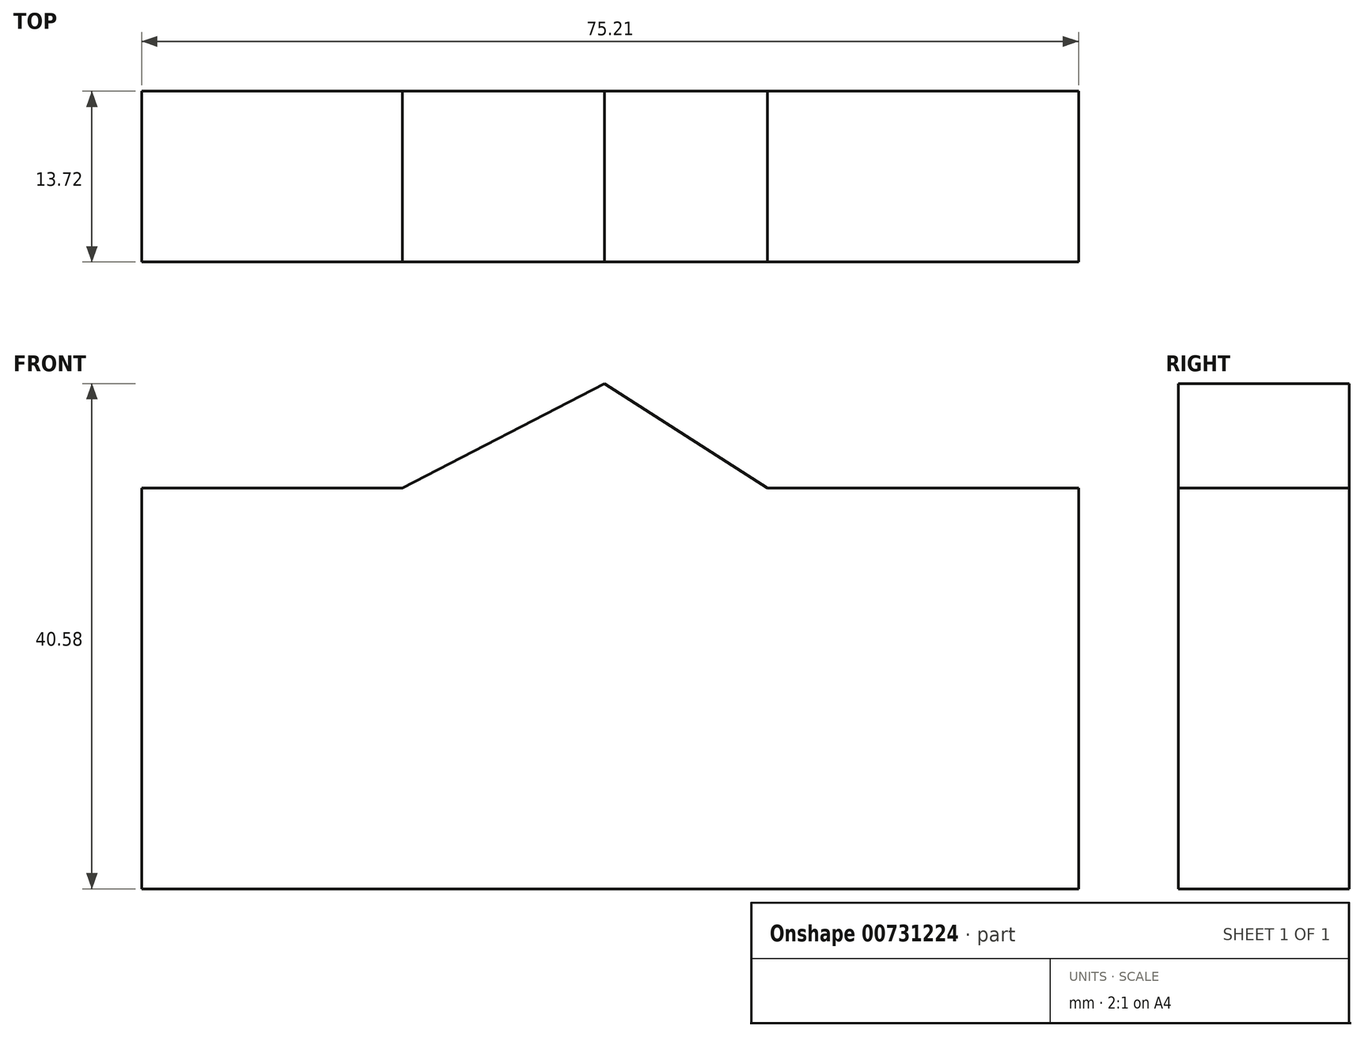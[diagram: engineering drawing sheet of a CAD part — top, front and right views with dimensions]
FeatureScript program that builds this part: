
annotation { "Feature Type Name" : "Feature", "Feature Type Description" : "" }
export const myFeature = defineFeature(function(context is Context, id is Id, definition is map)
    precondition{}
    {
        {
            var Q0;
            Q0=qCreatedBy(makeId("Front.planeOp"),FACE);
            var sketch = newSketch(context, id + "F0", { "sketchPlane" : qUnion([Q0])});
            skLineSegment(sketch, "E0.0", {"start": v(-40.04, 55.65) * mm, "end": v(-23.4, 64.25) * mm});
            skLineSegment(sketch, "E0.1", {"start": v(-23.4, 64.25) * mm, "end": v(-7.62, 54.13) * mm});
            skPoint(sketch, "E0.0.midPoint", {"position": v(-31.72, 59.95) * mm});
            skLineSegment(sketch, "E1.bottom", {"start": v(-60.55, 55.86) * mm, "end": v(14.66, 55.86) * mm});
            skLineSegment(sketch, "E1.top", {"start": v(-60.55, 23.67) * mm, "end": v(14.66, 23.67) * mm});
            skLineSegment(sketch, "E1.left", {"start": v(-60.55, 55.86) * mm, "end": v(-60.55, 23.67) * mm});
            skLineSegment(sketch, "E1.right", {"start": v(14.66, 55.86) * mm, "end": v(14.66, 23.67) * mm});
            skSolve(sketch);
        }
        {
            var Q0;
            Q0=makeQuery(id+"F0.imprint","IMPRINT",FACE,{"disambiguationData":[TD([[makeQuery(id+"F0.imprint","IMPRINT",EDGE,{"derivedFrom":sQuery(id+"F0.wireOp",EDGE,"E1.top")}),1.0]])]});
            var Q1;
            {var subQ0=sQuery(id+"F0.wireOp",EDGE,"E0.1");var subQ1=sQuery(id+"F0.wireOp",EDGE,"E0.0");var subQ2=makeQuery(id+"F0.imprint","INTERSECT",VERTEX,{"derivedFrom":[subQ1,subQ0]});Q1=makeQuery(id+"F0.imprint","IMPRINT",FACE,{"disambiguationData":[TD([[makeQuery(id+"F0.imprint","IMPRINT",EDGE,{"disambiguationData":[TD([[subQ2,1.0]])],"derivedFrom":subQ1}),-1.0]])]});}
            extrude(context, id + "F1", {"entities" : qUnion([Q0, Q1]), "depth" : 13.72 * mm, "offsetDistance" : 25.4 * mm});
        }
    });
